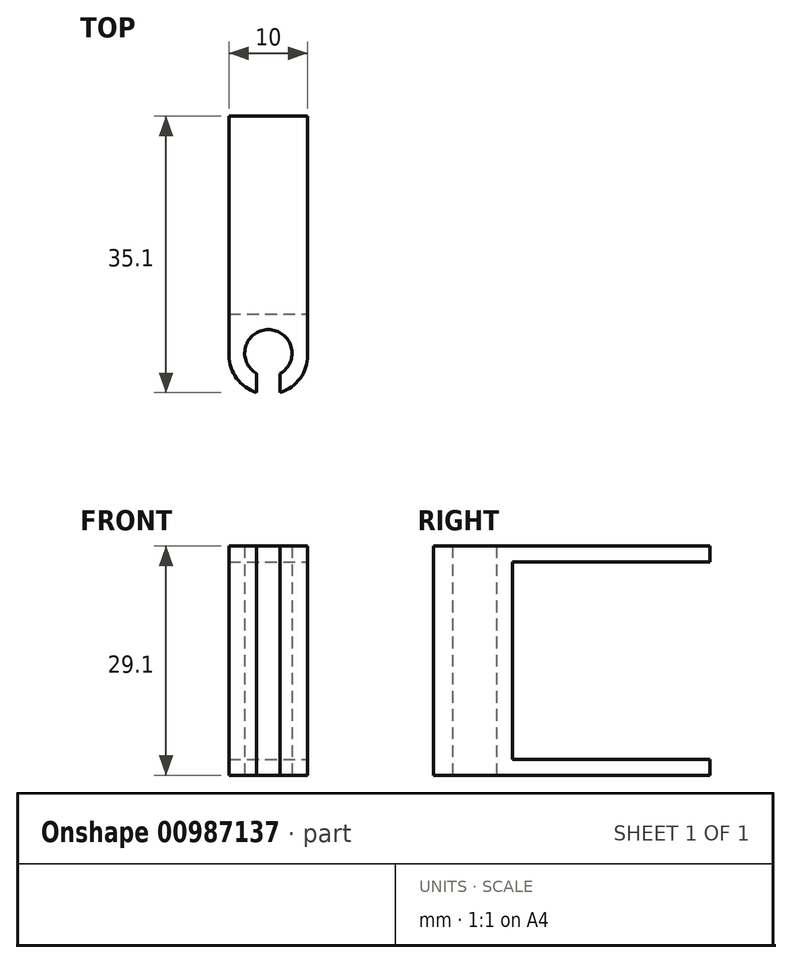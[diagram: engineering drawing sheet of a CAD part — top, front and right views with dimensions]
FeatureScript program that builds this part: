
annotation { "Feature Type Name" : "Feature", "Feature Type Description" : "" }
export const myFeature = defineFeature(function(context is Context, id is Id, definition is map)
    precondition{}
    {
        {
            assignVariable(context, id + "F0", {"name" : "CableDiameter", "anyValue" : 6});
        }
        {
            assignVariable(context, id + "F1", {"name" : "TableEdgeHeight", "anyValue" : 25.1});
        }
        {
            assignVariable(context, id + "F2", {"name" : "EdgeThickness", "anyValue" : 2});
        }
        {
            var Q0;
            Q0=qCreatedBy(makeId("Top.planeOp"),FACE);
            var sketch = newSketch(context, id + "F3", { "sketchPlane" : qUnion([Q0])});
            skLineSegment(sketch, "E0.bottom", {"start": v(-5, 12.55) * mm, "end": v(5, 12.55) * mm});
            skLineSegment(sketch, "E0.top", {"start": v(-5, -12.55) * mm, "end": v(5, -12.55) * mm});
            skLineSegment(sketch, "E0.left", {"start": v(-5, 12.55) * mm, "end": v(-5, -12.55) * mm});
            skLineSegment(sketch, "E0.right", {"start": v(5, 12.55) * mm, "end": v(5, -12.55) * mm});
            skLineSegment(sketch, "E1", {"start": v(0, 26.86) * mm, "end": v(0, -34.02) * mm, "construction": true});
            skLineSegment(sketch, "E2", {"start": v(-47.54, 0) * mm, "end": v(55.27, 0) * mm, "construction": true});
            skLineSegment(sketch, "E3.top", {"start": v(-5, -22.55) * mm, "end": v(-1.5, -22.55) * mm});
            skLineSegment(sketch, "E3.left", {"start": v(-5, -12.55) * mm, "end": v(-5, -22.55) * mm});
            skLineSegment(sketch, "E3.right", {"start": v(5, -12.55) * mm, "end": v(5, -22.55) * mm});
            skPoint(sketch, "E4", {"position": v(0, -22.55) * mm});
            skArc(sketch, "E5", {"start": v(1.5, -20.15) * mm, "mid": v(0, -14.55) * mm, "end": v(-1.5, -20.15) * mm});
            skPoint(sketch, "E5.centerSnap0", {"position": v(-5, -17.55) * mm});
            skLineSegment(sketch, "E6", {"start": v(-1.5, -20.15) * mm, "end": v(-1.5, -22.55) * mm});
            skLineSegment(sketch, "E7", {"start": v(1.5, -20.15) * mm, "end": v(1.5, -22.55) * mm});
            skLineSegment(sketch, "E8.trimOffspring", {"start": v(1.5, -22.55) * mm, "end": v(5, -22.55) * mm});
            skLineSegment(sketch, "E9", {"start": v(-1.5, -22.55) * mm, "end": v(1.5, -22.55) * mm, "construction": true});
            skSolve(sketch);
        }
        {
            var Q0;
            Q0=makeQuery(id+"F3.imprint","IMPRINT",FACE,{"disambiguationData":[TD([[makeQuery(id+"F3.imprint","IMPRINT",EDGE,{"derivedFrom":sQuery(id+"F3.wireOp",EDGE,"E0.bottom")}),-1.0]])]});
            var Q1;
            Q1=makeQuery(id+"F3.imprint","IMPRINT",FACE,{"disambiguationData":[TD([[makeQuery(id+"F3.imprint","IMPRINT",EDGE,{"derivedFrom":sQuery(id+"F3.wireOp",EDGE,"E0.top")}),-1.0]])]});
            extrude(context, id + "F4", {"entities" : qUnion([Q0, Q1]), "depth" : (getVariable(context, 'TableEdgeHeight') + (2 * getVariable(context, 'EdgeThickness'))) * mm, "offsetDistance" : 25 * mm});
        }
        {
            var Q0;
            Q0=makeQuery(id+"F3.imprint","IMPRINT",FACE,{"disambiguationData":[TD([[makeQuery(id+"F3.imprint","IMPRINT",EDGE,{"derivedFrom":sQuery(id+"F3.wireOp",EDGE,"E0.bottom")}),-1.0]])]});
            extrude(context, id + "F5", {"entities" : qUnion([Q0]), "operationType" : NewBodyOperationType.REMOVE, "depth" : (getVariable(context, 'TableEdgeHeight') + getVariable(context, 'EdgeThickness')) * mm, "offsetDistance" : 25 * mm});
        }
        {
            var Q0;
            Q0=makeQuery(id+"F3.imprint","IMPRINT",FACE,{"disambiguationData":[TD([[makeQuery(id+"F3.imprint","IMPRINT",EDGE,{"derivedFrom":sQuery(id+"F3.wireOp",EDGE,"E0.bottom")}),-1.0]])]});
            var Q1;
            Q1=makeQuery(id+"F3.imprint","IMPRINT",FACE,{"disambiguationData":[TD([[makeQuery(id+"F3.imprint","IMPRINT",EDGE,{"derivedFrom":sQuery(id+"F3.wireOp",EDGE,"E0.top")}),-1.0]])]});
            extrude(context, id + "F6", {"entities" : qUnion([Q0, Q1]), "operationType" : NewBodyOperationType.ADD, "depth" : (getVariable(context, 'EdgeThickness')) * mm, "offsetDistance" : 25 * mm});
        }
        {
            var Q0;
            Q0=makeQuery(id+"F4.opExtrude","SWEPT_EDGE",EDGE,{"disambiguationData":[OSD([sQuery(id+"F3.wireOp",EDGE,"E3.top"),sQuery(id+"F3.wireOp",EDGE,"E3.left")])]});
            var Q1;
            Q1=makeQuery(id+"F4.opExtrude","SWEPT_EDGE",EDGE,{"disambiguationData":[OSD([sQuery(id+"F3.wireOp",EDGE,"E3.right"),sQuery(id+"F3.wireOp",EDGE,"E8.trimOffspring")])]});
            fillet(context, id + "F7", {"entities" : qUnion([Q0, Q1]), "radius" : ((getVariable(context, 'CableDiameter') / 2) + getVariable(context, 'EdgeThickness')) * mm, "tangentPropagation" : true, "allowEdgeOverflow" : false});
        }
    });
